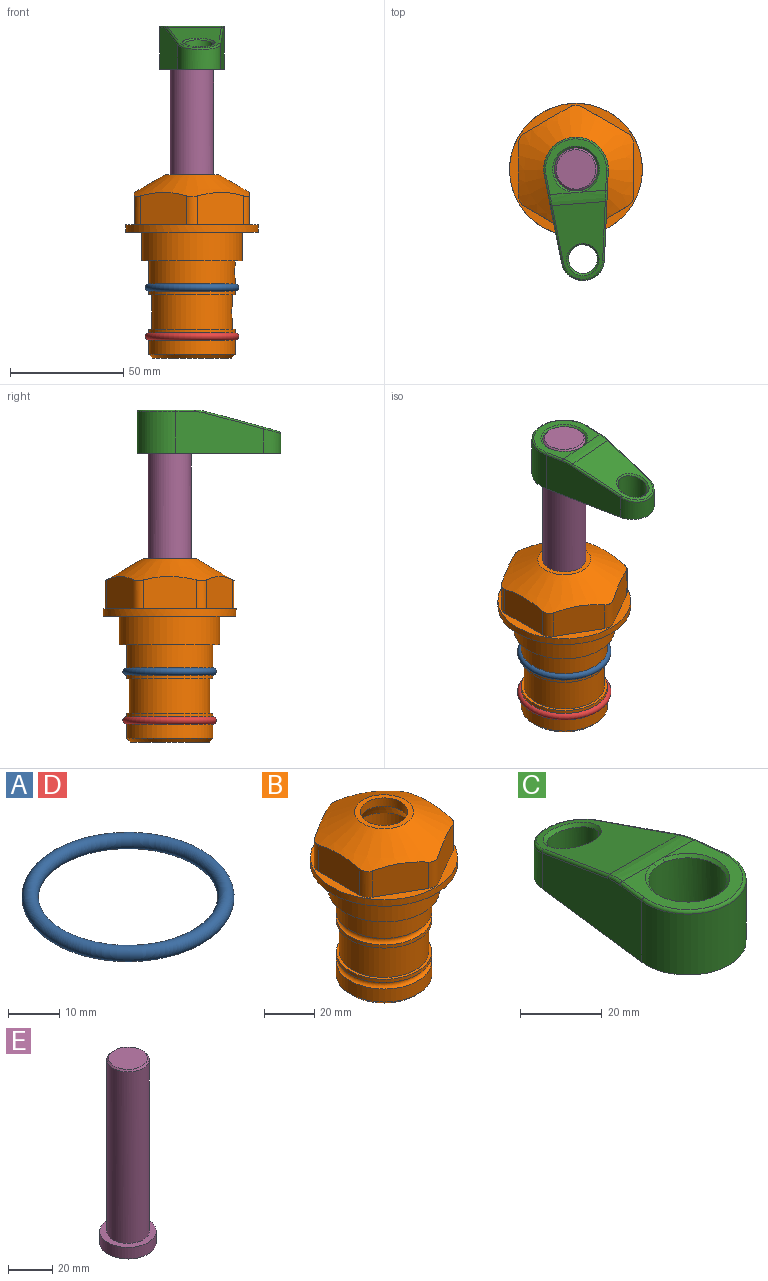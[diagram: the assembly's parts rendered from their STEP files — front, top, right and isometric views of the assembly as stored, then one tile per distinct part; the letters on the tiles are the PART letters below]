
ASSEMBLY  parts=5 mates=4
PART A: 1 faces, bbox 44.7x44.7x3.2 mm
  f0: torus R=19.05mm, axis (0,0,1), area 1193.9mm2
PART B: 36 faces, bbox 58.7x58.7x81 mm
  f0: cylinder r=17.78mm len=35.56mm, axis (0,0,1), area 1670.8mm2, adj f23,f24,f31
  f1: cylinder r=19.05mm len=38.1mm, axis (0,0,1), area 1191.9mm2, adj f26,f27,f30
  f2: plane 58.66x58.66mm, normal (0,0,-1), area 1150.6mm2, adj f3,f28
  f3: cylinder r=29.33mm len=58.66mm, axis (0,0,-1), area 585.1mm2, adj f2,f4
  f4: plane 58.66x58.66mm, normal (0,0,1), area 475.9mm2, adj f3,f5,f6,f7,f8,f9,f10,f11
  f5: plane 20.32x14.34mm, normal (-0.5,0.87,0), area 324.4mm2, adj f4,f15,f16,f17
  f6: plane 20.32x14.34mm, normal (0.5,0.87,0), area 324.4mm2, adj f4,f14,f15,f17
  f7: plane 23.48x14.34mm, normal (1,0,0), area 324.4mm2, adj f4,f13,f14,f17
  f8: plane 20.32x14.34mm, normal (0.5,-0.87,0), area 324.4mm2, adj f4,f12,f13,f17
  f9: plane 20.32x14.34mm, normal (-0.5,-0.87,0), area 324.4mm2, adj f4,f11,f12,f17
  f10: plane 23.48x14.34mm, normal (-1,0,0), area 324.4mm2, adj f4,f11,f16,f17
  f11: cylinder r=5.08mm len=12.85mm, axis (0,0,-1), area 67.2mm2, adj f4,f9,f10,f17
  f12: cylinder r=5.08mm len=12.85mm, axis (0,0,-1), area 67.2mm2, adj f4,f8,f9,f17
  f13: cylinder r=5.08mm len=12.85mm, axis (0,0,-1), area 67.2mm2, adj f4,f7,f8,f17
  f14: cylinder r=5.08mm len=12.85mm, axis (0,0,-1), area 67.2mm2, adj f4,f6,f7,f17
  f15: cylinder r=5.08mm len=12.85mm, axis (0,0,-1), area 67.2mm2, adj f4,f5,f6,f17
  f16: cylinder r=5.08mm len=12.85mm, axis (0,0,-1), area 67.2mm2, adj f4,f5,f10,f17
  f17: cone r=11.73mm half-angle=60deg, axis (0,0,-1), area 2071.8mm2, adj f5,f6,f7,f8,f9,f10,f11,f12
  f18: plane 23.46x23.46mm, normal (0,0,1), area 147.4mm2, adj f17,f35
  f19: plane 34.93x34.93mm, normal (0,0,-1), area 958mm2, adj f29
  f20: cylinder r=19.05mm len=38.1mm, axis (0,0,1), area 760.1mm2, adj f21,f29
  f21: torus R=19.05mm, axis (0,0,1), area 565.3mm2, adj f20,f22
  f22: cylinder r=19.05mm len=38.1mm, axis (0,0,1), area 190mm2, adj f21,f23
  f23: plane 38.1x38.1mm, normal (0,0,1), area 146.9mm2, adj f0,f22
  f24: plane 38.1x38.1mm, normal (0,0,-1), area 146.9mm2, adj f0,f25
  f25: cylinder r=19.05mm len=38.1mm, axis (0,0,1), area 190mm2, adj f24,f26
  f26: torus R=19.05mm, axis (0,0,1), area 565.3mm2, adj f1,f25
  f27: plane 44.45x44.45mm, normal (0,0,-1), area 411.7mm2, adj f1,f28
  f28: cylinder r=22.23mm len=44.45mm, axis (0,0,1), area 1773.5mm2, adj f2,f27
  f29: cone r=19.05mm half-angle=45deg, axis (0,0,1), area 257.5mm2, adj f19,f20
  f30: cylinder r=3.17mm len=6.75mm, axis (-1,0,0), area 128mm2, adj f1,f33
  f31: cylinder r=3.17mm len=6.35mm, axis (-1,0,0), area 102.5mm2, adj f0,f33
  f32: plane 25.4x25.4mm, normal (0,0,1), area 506.7mm2, adj f33
  f33: cylinder r=12.7mm len=66.42mm, axis (0,0,-1), area 5236.2mm2, adj f30,f31,f32,f34
  f34: cone r=9.53mm half-angle=30deg, axis (0,0,-1), area 443.4mm2, adj f33,f35
  f35: cylinder r=9.53mm len=19.05mm, axis (0,0,-1), area 240.9mm2, adj f18,f34
PART C: 31 faces, bbox 31.7x65.5x19.8 mm
  f0: plane 39.12x18.26mm, normal (0.99,0.12,0), area 612.2mm2, adj f1,f4,f7,f11,f13,f15
  f1: cylinder r=9.53mm len=18.91mm, axis (0,0,-1), area 296.1mm2, adj f0,f2,f7,f17
  f2: plane 39.12x18.26mm, normal (-0.99,0.12,0), area 612.2mm2, adj f1,f4,f7,f12,f14,f16
  f3: cylinder r=6.35mm len=12.7mm, axis (0,0,-1), area 362.4mm2, adj f7,f18
  f4: cylinder r=14.29mm len=28.58mm, axis (0,0,-1), area 882.2mm2, adj f0,f2,f7,f10
  f5: cylinder r=9.53mm len=19.05mm, axis (0,0,-1), area 1092.6mm2, adj f7,f19,f20
  f6: plane 26.99x23.69mm, normal (0,0,1), area 216.2mm2, adj f9,f10,f11,f12,f19
  f7: plane 63.5x28.58mm, normal (0,0,-1), area 661.8mm2, adj f0,f1,f2,f3,f4,f5,f22,f23
  f8: plane 33.52x23.6mm, normal (0,0.26,0.97), area 486mm2, adj f9,f15,f16,f17,f18
  f9: cylinder r=19.05mm len=24.72mm, axis (1,0,0), area 120.4mm2, adj f6,f8,f13,f14,f20
  f10: torus R=13.49mm, axis (0,0,1), area 59mm2, adj f4,f6,f11,f12
  f11: cylinder r=0.79mm len=8.67mm, axis (0.12,-0.99,0), area 10.8mm2, adj f0,f6,f10,f13
  f12: cylinder r=0.79mm len=8.67mm, axis (0.12,0.99,0), area 10.8mm2, adj f2,f6,f10,f14
  f13: bspline ~4.95x1.42mm, area 6.1mm2, adj f0,f9,f11,f15
  f14: bspline ~4.95x1.42mm, area 6.1mm2, adj f2,f9,f12,f16
  f15: cylinder r=0.79mm len=25.95mm, axis (0.12,-0.96,0.26), area 32.9mm2, adj f0,f8,f13,f17
  f16: cylinder r=0.79mm len=25.95mm, axis (0.12,0.96,-0.26), area 32.9mm2, adj f2,f8,f14,f17
  f17: bspline ~18.91x8.38mm, area 30mm2, adj f1,f8,f15,f16
  f18: bspline ~14.29x14.29mm, area 48.3mm2, adj f3,f8
  f19: cone r=9.53mm half-angle=45deg, axis (0,0,1), area 66.5mm2, adj f5,f6,f20
  f20: bspline ~3.22x0.96mm, area 3.5mm2, adj f5,f9,f19
  f21: plane 2.75x2.72mm, normal (0,0,-1), area 2.9mm2, adj f23,f25,f28
  f22: plane 23.05x15.88mm, normal (-0.99,-0.12,0), area 323.6mm2, adj f7,f25,f26,f27,f28,f29
  f23: plane 23.05x15.88mm, normal (0.99,-0.12,0), area 323.6mm2, adj f7,f21,f25,f27,f28,f30
  f24: cylinder r=9.53mm len=10.69mm, axis (0,0,-1), area 114.7mm2, adj f7,f27,f29,f30
  f25: cylinder r=12.7mm len=20.59mm, axis (0,0,-1), area 381.1mm2, adj f7,f21,f22,f23,f26,f28
  f26: plane 2.75x2.72mm, normal (0,0,-1), area 2.9mm2, adj f22,f25,f28
  f27: plane 19.72x18.37mm, normal (0,-0.26,-0.97), area 291.8mm2, adj f22,f23,f24,f28,f29,f30
  f28: cylinder r=15.88mm len=19.92mm, axis (1,0,0), area 54.8mm2, adj f21,f22,f23,f25,f26,f27
  f29: cylinder r=1.59mm len=11mm, axis (0,0,-1), area 34.7mm2, adj f7,f22,f24,f27
  f30: cylinder r=1.59mm len=11mm, axis (0,0,-1), area 34.7mm2, adj f7,f23,f24,f27
PART D: same geometry as A
PART E: 6 faces, bbox 25.4x25.4x101.6 mm
  f0: plane 17.46x17.46mm, normal (0,0,1), area 239.5mm2, adj f5
  f1: plane 25.4x25.4mm, normal (0,0,-1), area 506.7mm2, adj f2
  f2: cylinder r=12.7mm len=25.4mm, axis (0,0,1), area 506.7mm2, adj f1,f3
  f3: plane 25.4x25.4mm, normal (0,0,1), area 221.7mm2, adj f2,f4
  f4: cylinder r=9.53mm len=94.46mm, axis (0,0,1), area 5653mm2, adj f3,f5
  f5: cone r=8.73mm half-angle=45deg, axis (0,0,-1), area 64.4mm2, adj f0,f4
PLACE A at identity
PLACE B at identity fixed
PLACE C rot(axis=(0,0,-1),175.6deg) t=(0,0,27.55)mm
PLACE D t=(0,0,-21.59)mm
PLACE E rot(axis=(0,0,-1),175.6deg) t=(0,0,27.55)mm
MATE cylindrical E.f2 <-> B.f0  axis (0,0,1) through (0,0,-10.55)mm
MATE fastened A.f0 <-> B.f0  axis (0,0,1) through (0,0,-24.51)mm
MATE fastened E.f2 <-> C.f4  axis (0,0,1) through (0,0,91.05)mm
MATE fastened D.f0 <-> B.f0  axis (0,0,1) through (0,0,-46.1)mm
